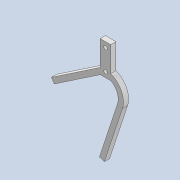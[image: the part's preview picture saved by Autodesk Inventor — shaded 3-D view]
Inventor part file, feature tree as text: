
AUTODESK INVENTOR PART (.ipt)
format: ipt  version: 2020 (Build 240168000, 168)  size: 264,192 bytes
history: native  units: mm
features: extrude x5, sketch x5, other x4, fillet x4, reference x4, projected_geometry x4, chamfer x3
ambient origin geometry x8: Origin, YZ Plane, XZ Plane, XY Plane, X Axis, Y Axis, Z Axis, Center Point
bodies: Solid1 (feature_tree)
feature tree (29):
  extrude  "Extrusion1"  Depth=6.0mm
  extrude  "Extrusion2"  Depth=2.0mm
  sketch  "Sketch3"  dims[d4=32.0mm d5=25.481807mm]
  other  "Work Point1"
  extrude  "Extrusion3"  Depth=25.481807mm
  extrude  "Extrusion4"  Depth=7.330383mm
  chamfer  "Chamfer1"  Distance=3.0mm
  extrude  "Extrusion5"  Depth=3.0mm
  fillet  "Fillet1"  Radius=0.078359mm
  fillet  "Fillet2"  Radius=7.6mm
  chamfer  "Chamfer2"  Distance=3.0mm
  chamfer  "Chamfer3"  Distance=2.5mm
  fillet  "Fillet3"  Radius=3.0mm
  fillet  "Fillet4"  Radius=14.5mm
  sketch  "Sketch1"  dims[d0=18.0mm d1=6.0mm]
  reference  "Reference1"
  reference  "Reference2"
  reference  "Reference3"
  reference  "Reference4"
  sketch  "Sketch2"  dims[d2=2.0mm d3=2.0mm]
  projected_geometry  "Projected Loop1"
  projected_geometry  "Projected Loop2"
  sketch  "Sketch4"  dims[d6=35.0mm d7=7.330383mm]
  projected_geometry  "Projected Loop3"
  projected_geometry  "Projected Loop4"
  sketch  "Sketch5"  dims[d8=8.0mm d9=3.0mm d10=3.0mm d11=0.078359mm d12=7.6mm d13=3.0mm d14=0.0mm d15=2.5mm d16=3.0mm d17=0.0mm d18=14.5mm d19=0.0mm d20=8.0mm d21=6.0mm d22=6.0mm d23=0.0mm d24=3.0mm d25=0.0mm d26=2.0mm d27=2.0mm d28=45.0deg d29=3.0mm d30=3.0mm d31=3.0mm d32=0.0mm d33=33.5mm d34=1.6mm d35=3.0mm d36=2.0mm d37=2.0mm d38=2.0mm d39=45.0deg d40=1.5mm d41=2.0mm d42=45.0deg d43=4.0mm d44=2.0mm]
  parser-record x1  (decoder bookkeeping rows leaked as tree rows — omitted from the tree; the rows remain in map.json)
  other  "driver_ass_1.iam"
  other  "stand_1:1"
note: 1 file-system path scrubbed to <path> (originals preserved in map.json)
